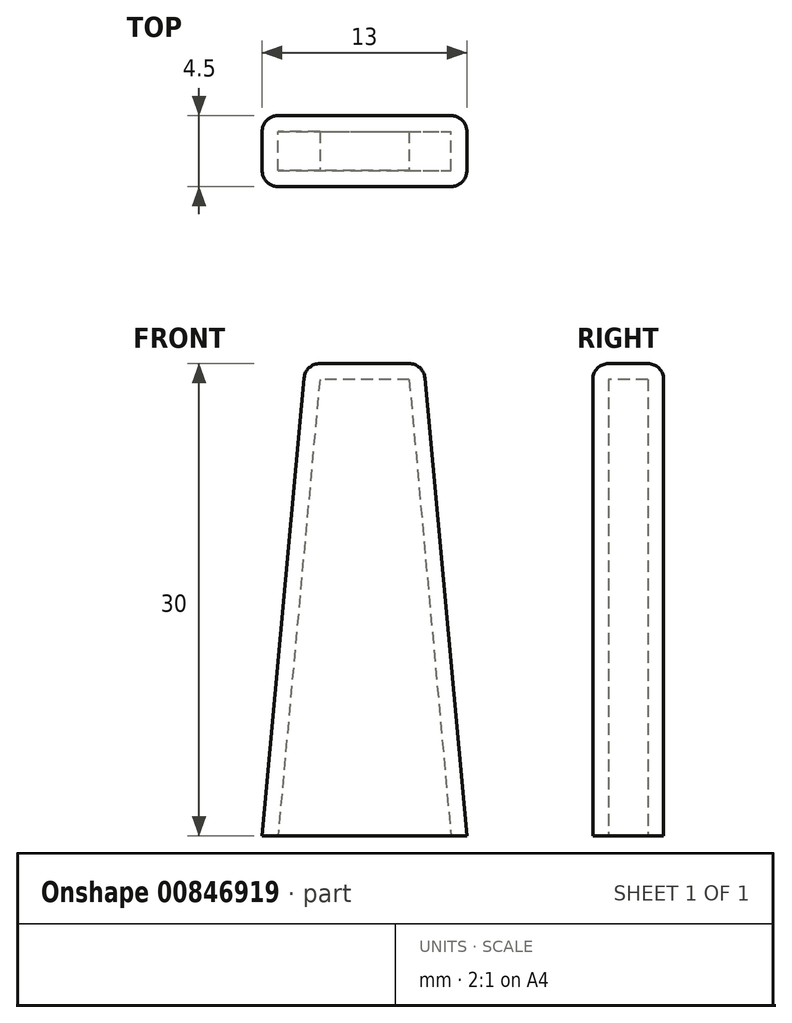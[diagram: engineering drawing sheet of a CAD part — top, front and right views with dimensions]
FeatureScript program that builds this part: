
annotation { "Feature Type Name" : "Feature", "Feature Type Description" : "" }
export const myFeature = defineFeature(function(context is Context, id is Id, definition is map)
    precondition{}
    {
        {
            var Q0;
            Q0=qCreatedBy(makeId("Front.planeOp"),FACE);
            var sketch = newSketch(context, id + "F0", { "sketchPlane" : qUnion([Q0])});
            skLineSegment(sketch, "E0", {"start": v(-6.5, 0) * mm, "end": v(6.5, 0) * mm});
            skLineSegment(sketch, "E1", {"start": v(6.5, 0) * mm, "end": v(3.75, 30) * mm});
            skLineSegment(sketch, "E2", {"start": v(3.75, 30) * mm, "end": v(-3.75, 30) * mm});
            skLineSegment(sketch, "E3", {"start": v(-3.75, 30) * mm, "end": v(-6.5, 0) * mm});
            skSolve(sketch);
        }
        {
            var Q0;
            Q0 = qSketchRegion(id + "F0", true);
            extrude(context, id + "F1", {"entities" : qUnion([Q0]), "endBound" : BoundingType.SYMMETRIC, "depth" : 4.5 * mm, "offsetDistance" : 25 * mm});
        }
        {
            var Q0;
            Q0=makeQuery(id+"F1.opExtrude","SWEPT_EDGE",EDGE,{"disambiguationData":[OSD([sQuery(id+"F0.wireOp",EDGE,"E2"),sQuery(id+"F0.wireOp",EDGE,"E3")])]});
            var Q1;
            Q1=makeQuery(id+"F1.opExtrude","SWEPT_EDGE",EDGE,{"disambiguationData":[OSD([sQuery(id+"F0.wireOp",EDGE,"E1"),sQuery(id+"F0.wireOp",EDGE,"E2")])]});
            var Q2;
            Q2=makeQuery(id+"F1.opExtrude","CAP_EDGE",EDGE,{"disambiguationData":[OSD([sQuery(id+"F0.wireOp",EDGE,"E1")])],"isStart":false});
            var Q3;
            Q3=makeQuery(id+"F1.opExtrude","CAP_EDGE",EDGE,{"disambiguationData":[OSD([sQuery(id+"F0.wireOp",EDGE,"E2")])],"isStart":false});
            var Q4;
            Q4=makeQuery(id+"F1.opExtrude","CAP_EDGE",EDGE,{"disambiguationData":[OSD([sQuery(id+"F0.wireOp",EDGE,"E3")])],"isStart":false});
            var Q5;
            Q5=makeQuery(id+"F1.opExtrude","CAP_EDGE",EDGE,{"disambiguationData":[OSD([sQuery(id+"F0.wireOp",EDGE,"E3")])],"isStart":true});
            var Q6;
            Q6=makeQuery(id+"F1.opExtrude","CAP_EDGE",EDGE,{"disambiguationData":[OSD([sQuery(id+"F0.wireOp",EDGE,"E1")])],"isStart":true});
            var Q7;
            Q7=makeQuery(id+"F1.opExtrude","CAP_EDGE",EDGE,{"disambiguationData":[OSD([sQuery(id+"F0.wireOp",EDGE,"E2")])],"isStart":true});
            fillet(context, id + "F2", {"entities" : qUnion([Q0, Q1, Q2, Q3, Q4, Q5, Q6, Q7]), "radius" : 1 * mm, "tangentPropagation" : true, "allowEdgeOverflow" : false});
        }
        {
            var Q0;
            Q0=makeQuery(id+"F1.opExtrude","SWEPT_FACE",FACE,{"disambiguationData":[OSD([sQuery(id+"F0.wireOp",EDGE,"E0")])]});
            shell(context, id + "F3", {"entities" : qUnion([Q0]), "thickness" : 1 * mm});
        }
    });
